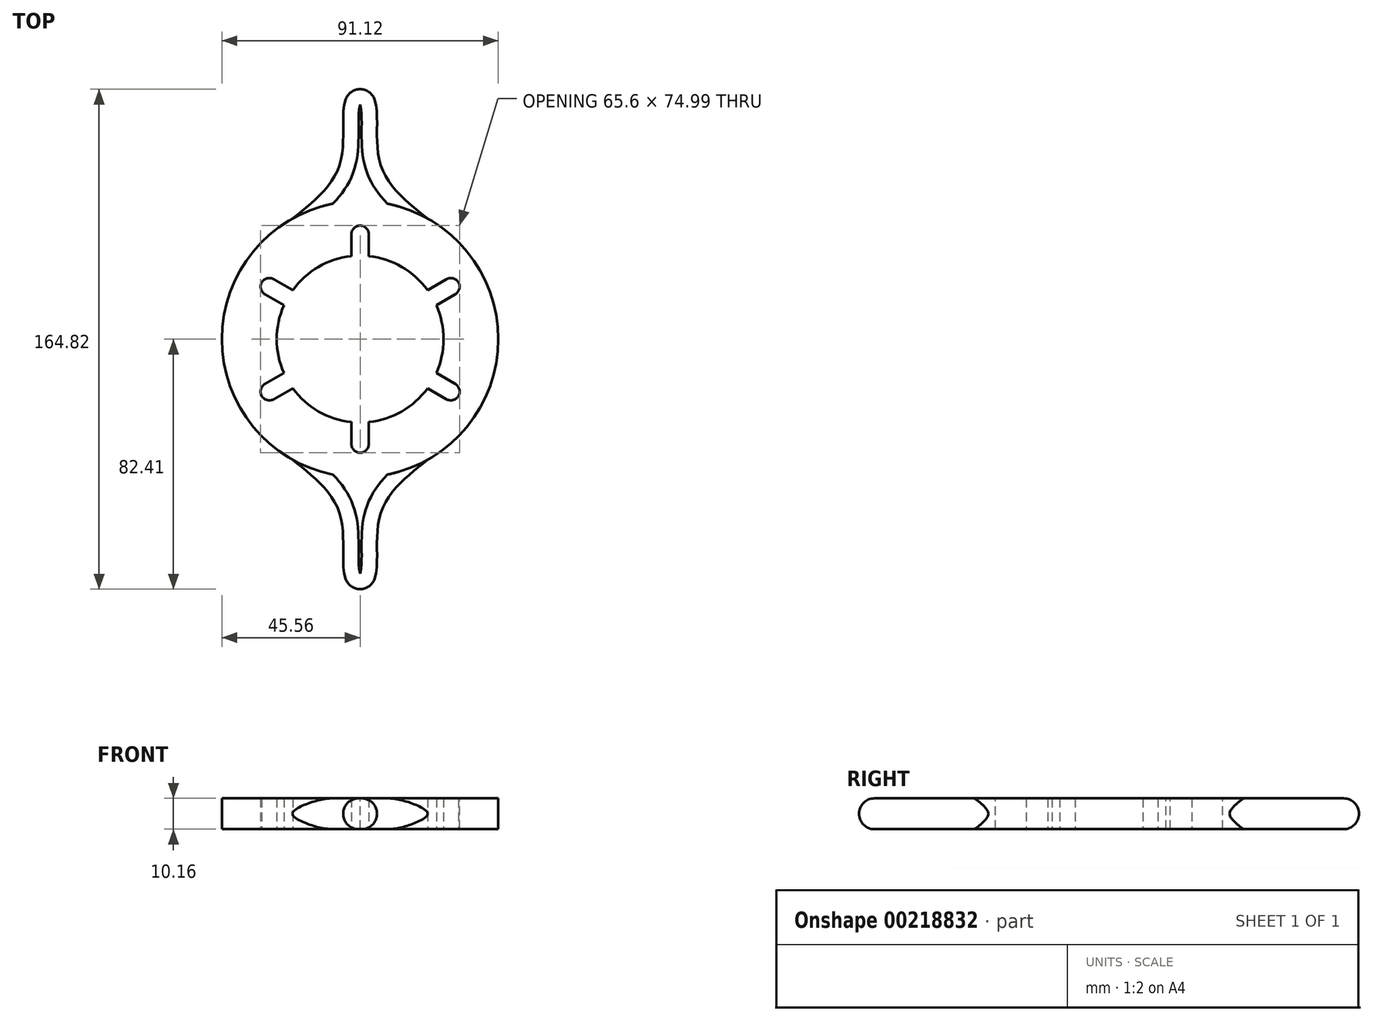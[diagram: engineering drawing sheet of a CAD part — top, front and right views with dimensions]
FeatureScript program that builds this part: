
annotation { "Feature Type Name" : "Feature", "Feature Type Description" : "" }
export const myFeature = defineFeature(function(context is Context, id is Id, definition is map)
    precondition{}
    {
        {
            var Q0;
            Q0=qCreatedBy(makeId("Top.planeOp"),FACE);
            var sketch = newSketch(context, id + "F0", { "sketchPlane" : qUnion([Q0])});
            skCircle(sketch, "E0", {"center": v(0, 0) * mm, "radius": 27.5 * mm});
            skLineSegment(sketch, "E1.bottom", {"start": v(2.9, 37.5) * mm, "end": v(-2.9, 37.5) * mm});
            skLineSegment(sketch, "E1.top", {"start": v(2.9, 17.5) * mm, "end": v(-2.9, 17.5) * mm});
            skLineSegment(sketch, "E1.left", {"start": v(2.9, 37.5) * mm, "end": v(2.9, 17.5) * mm});
            skLineSegment(sketch, "E1.right", {"start": v(-2.9, 37.5) * mm, "end": v(-2.9, 17.5) * mm});
            skPoint(sketch, "E1.middle", {"position": v(0, 27.5) * mm});
            skLineSegment(sketch, "E2.1.0", {"start": v(-31.02, 21.26) * mm, "end": v(-33.93, 16.24) * mm});
            skLineSegment(sketch, "E2.1.1", {"start": v(-33.93, 16.24) * mm, "end": v(-16.6, 6.24) * mm});
            skLineSegment(sketch, "E2.1.2", {"start": v(-31.02, 21.26) * mm, "end": v(-13.7, 11.26) * mm});
            skLineSegment(sketch, "E2.2.0", {"start": v(-33.93, -16.24) * mm, "end": v(-31.02, -21.26) * mm});
            skLineSegment(sketch, "E2.2.1", {"start": v(-31.02, -21.26) * mm, "end": v(-13.7, -11.26) * mm});
            skLineSegment(sketch, "E2.2.2", {"start": v(-33.93, -16.24) * mm, "end": v(-16.6, -6.24) * mm});
            skLineSegment(sketch, "E2.3.0", {"start": v(-2.9, -37.5) * mm, "end": v(2.9, -37.5) * mm});
            skLineSegment(sketch, "E2.3.1", {"start": v(2.9, -37.5) * mm, "end": v(2.9, -17.5) * mm});
            skLineSegment(sketch, "E2.3.2", {"start": v(-2.9, -37.5) * mm, "end": v(-2.9, -17.5) * mm});
            skLineSegment(sketch, "E2.4.0", {"start": v(31.02, -21.26) * mm, "end": v(33.93, -16.24) * mm});
            skLineSegment(sketch, "E2.4.1", {"start": v(33.93, -16.24) * mm, "end": v(16.6, -6.24) * mm});
            skLineSegment(sketch, "E2.4.2", {"start": v(31.02, -21.26) * mm, "end": v(13.7, -11.26) * mm});
            skLineSegment(sketch, "E2.5.0", {"start": v(33.93, 16.24) * mm, "end": v(31.02, 21.26) * mm});
            skLineSegment(sketch, "E2.5.1", {"start": v(31.02, 21.26) * mm, "end": v(13.7, 11.26) * mm});
            skLineSegment(sketch, "E2.5.2", {"start": v(33.93, 16.24) * mm, "end": v(16.6, 6.24) * mm});
            skCircle(sketch, "E3", {"center": v(0, 0) * mm, "radius": 45.56 * mm});
            skFitSpline(sketch, "E4", {"points": [v(22.33, -39.72) * mm, v(6.67, -57.74) * mm, v(5.02, -78.27) * mm, v(0, -84.76) * mm], "startDerivative": vector(-50.6, -40.11) * mm, "endDerivative": vector(-26.88, -21.53) * mm});
            skLineSegment(sketch, "E5", {"start": v(-45.56, 0) * mm, "end": v(45.56, 0) * mm});
            skFitSpline(sketch, "E6.MirrorCS", {"points": [v(22.33, 39.72) * mm, v(6.67, 57.74) * mm, v(5.02, 78.27) * mm, v(0, 84.76) * mm], "startDerivative": vector(-50.6, 40.11) * mm, "endDerivative": vector(-26.88, 21.53) * mm});
            skLineSegment(sketch, "E7", {"start": v(0, 84.76) * mm, "end": v(0, -84.76) * mm});
            skFitSpline(sketch, "E8.MirrorCS", {"points": [v(-22.33, -39.72) * mm, v(-6.67, -57.74) * mm, v(-5.02, -78.27) * mm, v(0, -84.76) * mm], "startDerivative": vector(50.6, -40.11) * mm, "endDerivative": vector(26.88, -21.53) * mm});
            skFitSpline(sketch, "E9.MirrorCS", {"points": [v(-22.33, 39.72) * mm, v(-6.67, 57.74) * mm, v(-5.02, 78.27) * mm, v(0, 84.76) * mm], "startDerivative": vector(50.6, 40.11) * mm, "endDerivative": vector(26.88, 21.53) * mm});
            skSolve(sketch);
        }
        {
            var Q0;
            {var subQ25=sQuery(id+"F0.wireOp",EDGE,"E1.bottom");Q0=makeQuery(id+"F0.imprint","IMPRINT",FACE,{"disambiguationData":[TD([[makeQuery(id+"F0.imprint","IMPRINT",EDGE,{"derivedFrom":subQ25}),-1.0]])]});}
            var Q1;
            {var subQ5=sQuery(id+"F0.wireOp",EDGE,"E2.4.0");Q1=makeQuery(id+"F0.imprint","IMPRINT",FACE,{"disambiguationData":[TD([[makeQuery(id+"F0.imprint","IMPRINT",EDGE,{"derivedFrom":subQ5}),-1.0]])]});}
            var Q2;
            {var subQ13=sQuery(id+"F0.wireOp",EDGE,"E2.2.0");Q2=makeQuery(id+"F0.imprint","IMPRINT",FACE,{"disambiguationData":[TD([[makeQuery(id+"F0.imprint","IMPRINT",EDGE,{"derivedFrom":subQ13}),-1.0]])]});}
            var Q3;
            {var subQ0=sQuery(id+"F0.wireOp",EDGE,"E9.MirrorCS");Q3=makeQuery(id+"F0.imprint","IMPRINT",FACE,{"disambiguationData":[TD([[makeQuery(id+"F0.imprint","IMPRINT",EDGE,{"derivedFrom":subQ0}),-1.0]])]});}
            var Q4;
            {var subQ0=sQuery(id+"F0.wireOp",EDGE,"E6.MirrorCS");Q4=makeQuery(id+"F0.imprint","IMPRINT",FACE,{"disambiguationData":[TD([[makeQuery(id+"F0.imprint","IMPRINT",EDGE,{"derivedFrom":subQ0}),1.0]])]});}
            var Q5;
            {var subQ0=sQuery(id+"F0.wireOp",EDGE,"E8.MirrorCS");Q5=makeQuery(id+"F0.imprint","IMPRINT",FACE,{"disambiguationData":[TD([[makeQuery(id+"F0.imprint","IMPRINT",EDGE,{"derivedFrom":subQ0}),1.0]])]});}
            var Q6;
            {var subQ0=sQuery(id+"F0.wireOp",EDGE,"E4");Q6=makeQuery(id+"F0.imprint","IMPRINT",FACE,{"disambiguationData":[TD([[makeQuery(id+"F0.imprint","IMPRINT",EDGE,{"derivedFrom":subQ0}),-1.0]])]});}
            extrude(context, id + "F1", {"entities" : qUnion([Q0, Q1, Q2, Q3, Q4, Q5, Q6]), "depth" : 10.16 * mm});
        }
        {
            var Q0;
            Q0=makeQuery(id+"F1.opExtrude","SWEPT_EDGE",EDGE,{"disambiguationData":[OSD([sQuery(id+"F0.wireOp",EDGE,"E2.1.0"),sQuery(id+"F0.wireOp",EDGE,"E2.1.2")])]});
            var Q1;
            Q1=makeQuery(id+"F1.opExtrude","SWEPT_EDGE",EDGE,{"disambiguationData":[OSD([sQuery(id+"F0.wireOp",EDGE,"E2.1.0"),sQuery(id+"F0.wireOp",EDGE,"E2.1.1")])]});
            var Q2;
            Q2=makeQuery(id+"F1.opExtrude","SWEPT_EDGE",EDGE,{"disambiguationData":[OSD([sQuery(id+"F0.wireOp",EDGE,"E1.bottom"),sQuery(id+"F0.wireOp",EDGE,"E1.right")])]});
            var Q3;
            Q3=makeQuery(id+"F1.opExtrude","SWEPT_EDGE",EDGE,{"disambiguationData":[OSD([sQuery(id+"F0.wireOp",EDGE,"E1.bottom"),sQuery(id+"F0.wireOp",EDGE,"E1.left")])]});
            var Q4;
            Q4=makeQuery(id+"F1.opExtrude","SWEPT_EDGE",EDGE,{"disambiguationData":[OSD([sQuery(id+"F0.wireOp",EDGE,"E2.5.0"),sQuery(id+"F0.wireOp",EDGE,"E2.5.1")])]});
            var Q5;
            Q5=makeQuery(id+"F1.opExtrude","SWEPT_EDGE",EDGE,{"disambiguationData":[OSD([sQuery(id+"F0.wireOp",EDGE,"E2.5.0"),sQuery(id+"F0.wireOp",EDGE,"E2.5.2")])]});
            var Q6;
            Q6=makeQuery(id+"F1.opExtrude","SWEPT_EDGE",EDGE,{"disambiguationData":[OSD([sQuery(id+"F0.wireOp",EDGE,"E2.2.0"),sQuery(id+"F0.wireOp",EDGE,"E2.2.2")])]});
            var Q7;
            Q7=makeQuery(id+"F1.opExtrude","SWEPT_EDGE",EDGE,{"disambiguationData":[OSD([sQuery(id+"F0.wireOp",EDGE,"E2.2.0"),sQuery(id+"F0.wireOp",EDGE,"E2.2.1")])]});
            var Q8;
            Q8=makeQuery(id+"F1.opExtrude","SWEPT_EDGE",EDGE,{"disambiguationData":[OSD([sQuery(id+"F0.wireOp",EDGE,"E2.4.0"),sQuery(id+"F0.wireOp",EDGE,"E2.4.2")])]});
            var Q9;
            Q9=makeQuery(id+"F1.opExtrude","SWEPT_EDGE",EDGE,{"disambiguationData":[OSD([sQuery(id+"F0.wireOp",EDGE,"E2.4.0"),sQuery(id+"F0.wireOp",EDGE,"E2.4.1")])]});
            var Q10;
            Q10=makeQuery(id+"F1.opExtrude","SWEPT_EDGE",EDGE,{"disambiguationData":[OSD([sQuery(id+"F0.wireOp",EDGE,"E2.3.0"),sQuery(id+"F0.wireOp",EDGE,"E2.3.1")])]});
            var Q11;
            Q11=makeQuery(id+"F1.opExtrude","SWEPT_EDGE",EDGE,{"disambiguationData":[OSD([sQuery(id+"F0.wireOp",EDGE,"E2.3.0"),sQuery(id+"F0.wireOp",EDGE,"E2.3.2")])]});
            fillet(context, id + "F2", {"entities" : qUnion([Q0, Q1, Q2, Q3, Q4, Q5, Q6, Q7, Q8, Q9, Q10, Q11]), "radius" : 3.05 * mm, "tangentPropagation" : true, "allowEdgeOverflow" : false});
        }
        {
            var Q0;
            Q0=makeQuery(id+"F1.opExtrude","CAP_EDGE",EDGE,{"disambiguationData":[OSD([sQuery(id+"F0.wireOp",EDGE,"E4")])],"isStart":false});
            var Q1;
            Q1=makeQuery(id+"F1.opExtrude","CAP_EDGE",EDGE,{"disambiguationData":[OSD([sQuery(id+"F0.wireOp",EDGE,"E4")])],"isStart":true});
            var Q2;
            Q2=makeQuery(id+"F1.opExtrude","CAP_EDGE",EDGE,{"disambiguationData":[OSD([sQuery(id+"F0.wireOp",EDGE,"E8.MirrorCS")])],"isStart":false});
            var Q3;
            Q3=makeQuery(id+"F1.opExtrude","CAP_EDGE",EDGE,{"disambiguationData":[OSD([sQuery(id+"F0.wireOp",EDGE,"E8.MirrorCS")])],"isStart":true});
            var Q4;
            Q4=makeQuery(id+"F1.opExtrude","SWEPT_EDGE",EDGE,{"disambiguationData":[OSD([sQuery(id+"F0.wireOp",EDGE,"E4"),sQuery(id+"F0.wireOp",EDGE,"E7"),sQuery(id+"F0.wireOp",EDGE,"E8.MirrorCS")])]});
            var Q5;
            Q5=makeQuery(id+"F1.opExtrude","CAP_EDGE",EDGE,{"disambiguationData":[OSD([sQuery(id+"F0.wireOp",EDGE,"E6.MirrorCS")])],"isStart":false});
            var Q6;
            Q6=makeQuery(id+"F1.opExtrude","CAP_EDGE",EDGE,{"disambiguationData":[OSD([sQuery(id+"F0.wireOp",EDGE,"E9.MirrorCS")])],"isStart":false});
            var Q7;
            Q7=makeQuery(id+"F1.opExtrude","SWEPT_EDGE",EDGE,{"disambiguationData":[OSD([sQuery(id+"F0.wireOp",EDGE,"E6.MirrorCS"),sQuery(id+"F0.wireOp",EDGE,"E7"),sQuery(id+"F0.wireOp",EDGE,"E9.MirrorCS")])]});
            var Q8;
            Q8=makeQuery(id+"F1.opExtrude","CAP_EDGE",EDGE,{"disambiguationData":[OSD([sQuery(id+"F0.wireOp",EDGE,"E6.MirrorCS")])],"isStart":true});
            var Q9;
            Q9=makeQuery(id+"F1.opExtrude","CAP_EDGE",EDGE,{"disambiguationData":[OSD([sQuery(id+"F0.wireOp",EDGE,"E9.MirrorCS")])],"isStart":true});
            fillet(context, id + "F3", {"entities" : qUnion([Q0, Q1, Q2, Q3, Q4, Q5, Q6, Q7, Q8, Q9]), "radius" : 5.08 * mm, "tangentPropagation" : true, "allowEdgeOverflow" : false});
        }
    });
